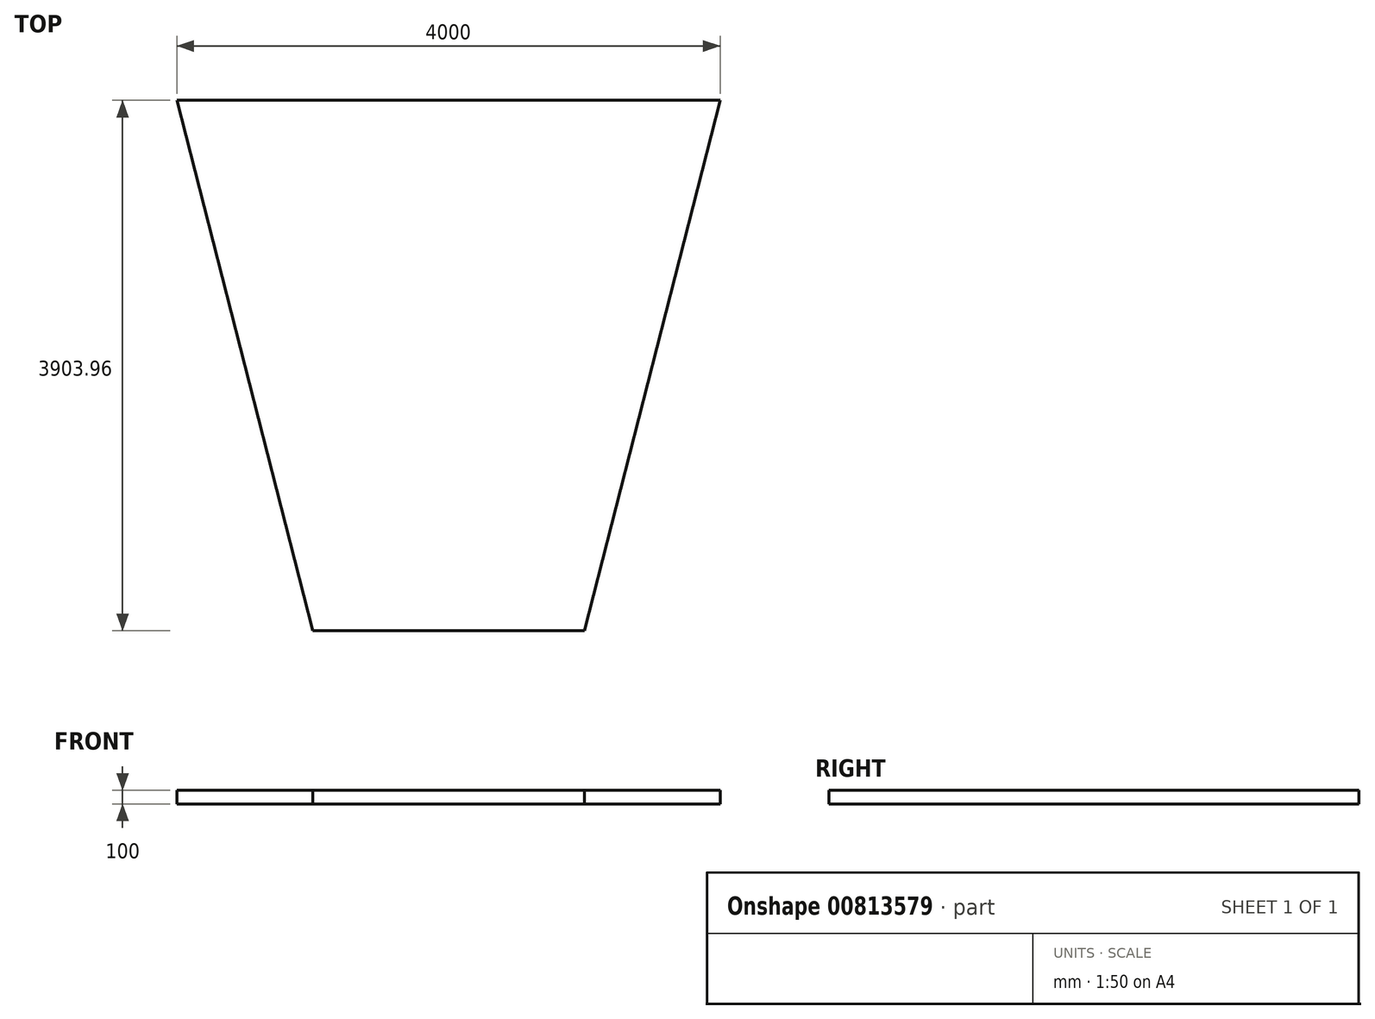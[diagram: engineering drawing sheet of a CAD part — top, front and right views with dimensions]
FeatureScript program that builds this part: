
annotation { "Feature Type Name" : "Feature", "Feature Type Description" : "" }
export const myFeature = defineFeature(function(context is Context, id is Id, definition is map)
    precondition{}
    {
        {
            var Q0;
            Q0=qCreatedBy(makeId("Top.planeOp"),FACE);
            var sketch = newSketch(context, id + "F0", { "sketchPlane" : qUnion([Q0])});
            skLineSegment(sketch, "E0", {"start": v(-2459.26, 3903.96) * mm, "end": v(1540.74, 3903.96) * mm});
            skLineSegment(sketch, "E1", {"start": v(1540.74, 3903.96) * mm, "end": v(540.74, 0) * mm});
            skLineSegment(sketch, "E2", {"start": v(540.74, 0) * mm, "end": v(-1459.26, 0) * mm});
            skLineSegment(sketch, "E3", {"start": v(-1459.26, 0) * mm, "end": v(-2459.26, 3903.96) * mm});
            skSolve(sketch);
        }
        {
            var Q0;
            Q0=makeQuery(id+"F0.imprint","IMPRINT",FACE,{"disambiguationData":[TD([[makeQuery(id+"F0.imprint","IMPRINT",EDGE,{"derivedFrom":sQuery(id+"F0.wireOp",EDGE,"E0")}),-1.0]])]});
            extrude(context, id + "F1", {"entities" : qUnion([Q0]), "depth" : 100 * mm, "offsetDistance" : 25 * mm});
        }
    });
